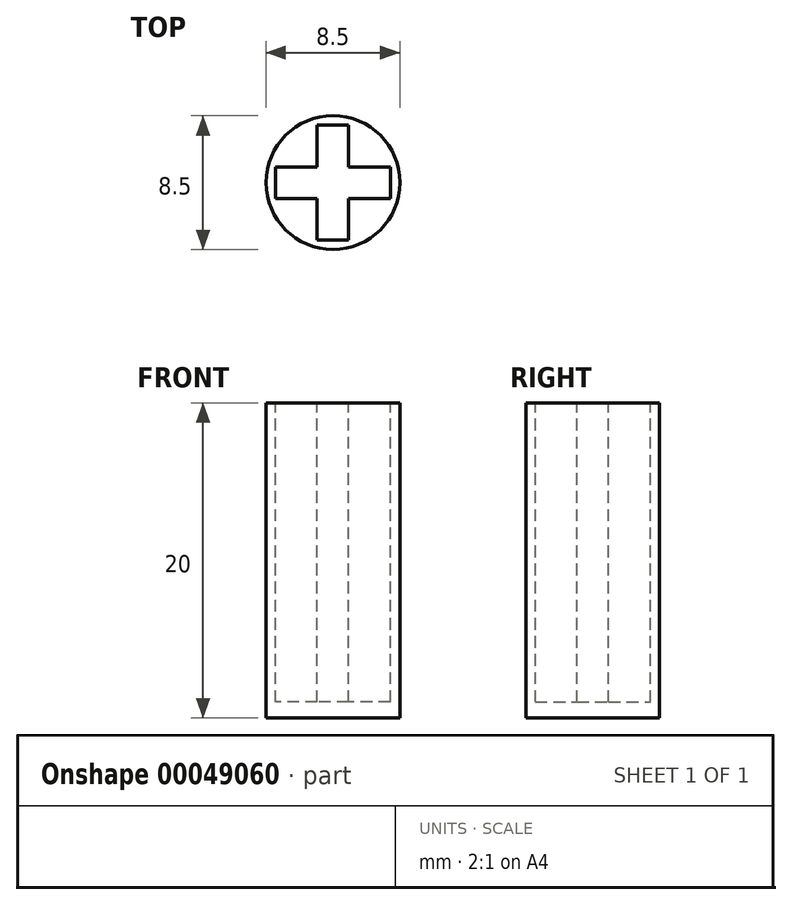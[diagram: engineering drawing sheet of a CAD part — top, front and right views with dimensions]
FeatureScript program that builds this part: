
annotation { "Feature Type Name" : "Feature", "Feature Type Description" : "" }
export const myFeature = defineFeature(function(context is Context, id is Id, definition is map)
    precondition{}
    {
        {
            var Q0;
            Q0=qCreatedBy(makeId("Top.planeOp"),FACE);
            var sketch = newSketch(context, id + "F0", { "sketchPlane" : qUnion([Q0])});
            skCircle(sketch, "E0", {"center": v(0, 0) * mm, "radius": 4.25 * mm});
            skSolve(sketch);
        }
        {
            var Q0;
            Q0 = qSketchRegion(id + "F0", true);
            extrude(context, id + "F1", {"entities" : qUnion([Q0]), "depth" : 20 * mm});
        }
        {
            var Q0;
            Q0=makeQuery(id+"F1.opExtrude","CAP_FACE",FACE,{"disambiguationData":[OSD([sQuery(id+"F0.wireOp",EDGE,"E0")])],"isStart":false});
            var sketch = newSketch(context, id + "F2", { "sketchPlane" : qUnion([Q0])});
            skLineSegment(sketch, "E1.rect.bottom", {"start": v(3.65, -1) * mm, "end": v(-3.65, -1) * mm});
            skLineSegment(sketch, "E1.rect.top", {"start": v(3.65, 1) * mm, "end": v(-3.65, 1) * mm});
            skLineSegment(sketch, "E1.rect.left", {"start": v(3.65, -1) * mm, "end": v(3.65, 1) * mm});
            skLineSegment(sketch, "E1.rect.right", {"start": v(-3.65, -1) * mm, "end": v(-3.65, 1) * mm});
            skPoint(sketch, "E1.rect.middle", {"position": v(0, 0) * mm});
            skLineSegment(sketch, "E2.rect.bottom", {"start": v(1, -3.65) * mm, "end": v(-1, -3.65) * mm});
            skLineSegment(sketch, "E2.rect.top", {"start": v(1, 3.65) * mm, "end": v(-1, 3.65) * mm});
            skLineSegment(sketch, "E2.rect.left", {"start": v(1, -3.65) * mm, "end": v(1, 3.65) * mm});
            skLineSegment(sketch, "E2.rect.right", {"start": v(-1, -3.65) * mm, "end": v(-1, 3.65) * mm});
            skSolve(sketch);
        }
        {
            var Q0;
            Q0 = qSketchRegion(id + "F2", true);
            var Q1;
            {var subQ5=sQuery(id+"F2.wireOp",EDGE,"E1.rect.right");Q1=makeQuery(id+"F2.imprint","IMPRINT",FACE,{"disambiguationData":[TD([[makeQuery(id+"F2.imprint","IMPRINT",EDGE,{"derivedFrom":subQ5}),-1.0]])]});}
            extrude(context, id + "F3", {"entities" : qUnion([Q0, Q1]), "operationType" : NewBodyOperationType.REMOVE, "oppositeDirection" : true, "depth" : 19 * mm});
        }
    });
